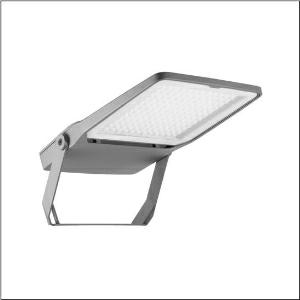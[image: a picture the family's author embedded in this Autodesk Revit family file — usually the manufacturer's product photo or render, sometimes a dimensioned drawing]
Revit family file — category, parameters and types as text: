
# Revit family: floodlight_fl_20_midi___rs17_5xa7682d1b1ac_4d76
name_source: partatom
category: Lighting Fixtures
units: mm (PartAtom-declared; Revit-internal decimal feet)

## family parameters
Cut with Voids When Loaded = No
Host = Face
Light Source = No
Part Type = Normal
Room Calculation Point = No
Round Connector Dimension = Use Diameter
Shared = No

## types (1)
- --- (1 x LED 3000K / CRI = 80 (unbekannt), 15350 lm, 3000K)
    Apparent Load = 142 VA
    CIE Flux Codes = 79 92 99 100 100
    Color Rendering = 80
    Color Temperature = 3000K
    Default Elevation = 1800 mm
    Description = Floodlight FL 20 midi, floodlight, primary light control with lens, of plastic, primary optical cover: protective disc, of toughened safety glass, transparent, light distribution: RS17, light emission: direct distribution, primary light characteristic: rotationally symmetric, installation type: surface-mounted, LED, High Power LED, rated luminous flux: 15.350lm, luminous efficacy: 108lm/W, light colour: 830, colour temperature: 3000K, control gear: ECG Plus, control: flexible luminous flux parameterisation, time-dependent luminous flux control, digital communication interface, power reduction, overheat protection, electronic power reduction, with terminal, 5-pole, max. 2.5mm², mains connection: 220..240V, AC, 50/60Hz, rated input power: 142W, LED unit, of diecast aluminium, powder-coated, Siteco® metallic grey (DB 702S), corrosivity category C5 mid according to DIN EN ISO 12944, incl. 1x M20 cable gland for cable Ø 6.5..12mm, length: 654mm, width: 450mm, height: 76mm, housing frame, of diecast aluminium, powder-coated, Siteco® metallic grey (DB 702S), mounting bracket, of steel, powder-coated, Siteco® metallic grey (DB 702S), DALI, protection rating (complete): IP66, insulation class (complete): insulation class II (safety insulation), certification: CE, ENEC, VDE, protection symbol: D, permissible operating ambient temperature: -40..+40°C, permissible operating ambient temperature for outdoor applications: -40..+50°C, standard: DIN EN 12944, packaging unit: 1 piece

Light Distribution: RS17
    Height = 76 mm
    Lamp = 1 x LED 3000K / CRI >= 80 (unbekannt)
    Lamp Light Flux = 15350 lm
    Lamp count = 1
    Length = 672 mm
    Luminous efficacy = 108 lm/W
    Manufacturer = Siteco
    ModVariant = No
    Model = 5XA7682D1B1AC
    Mounting Place = Wall
    Mounting Type = Surface mounted
    Number of Poles = 1
    OnlyDefault = Yes
    Power Factor = 1
    Product Name = Floodlight FL 20 midi | RS17
    Product group = floodlight | wall mounted
    ProductGroupID = 2001
    Protection Class = Protection class II
    Protection Degree = IP 66
    RLX_Detail_Level = 1
    RLX_Emergency_Light_Flux = 0 lm
    RLX_Emergency_Type = 0
    RLX_Emergency_Type_DB = No
    RlxData = <blob elided: 92325 chars, md5=02eca99a>
    Socket = socket
    Standby Power = 0 W
    System Light Flux = 15350 lm
    System Power = 142 W
    Type Comments = factory setting: luminous flux: 100 % | dim-lin: 254 | 489 mA
    Type Image = l_1005943.jpg
    URL = http://relux.com
    VarID = @adj_146737
    Voltage = 0 V
    Weight = 0.00 kg
    Width = 450 mm

## geometry (parser evidence)
native form markers: Blend x4, Sweep x12
no freeform markers — native parametric forms only
